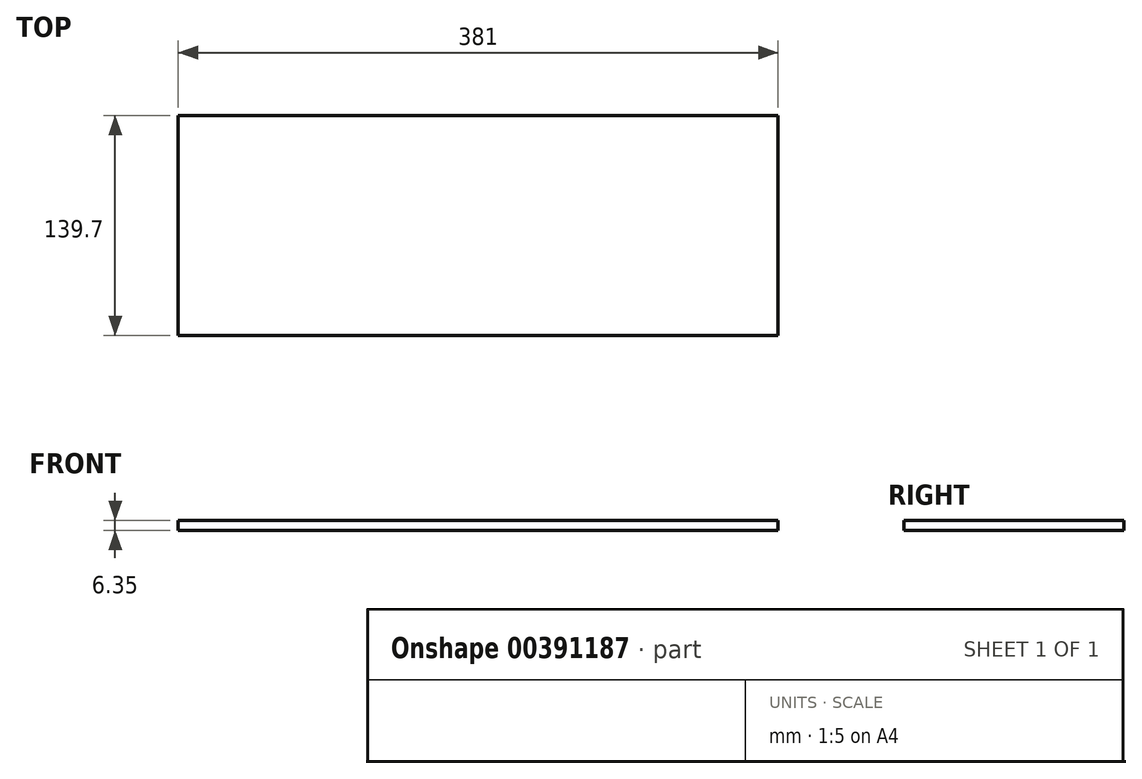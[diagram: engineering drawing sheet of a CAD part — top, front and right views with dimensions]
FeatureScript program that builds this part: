
annotation { "Feature Type Name" : "Feature", "Feature Type Description" : "" }
export const myFeature = defineFeature(function(context is Context, id is Id, definition is map)
    precondition{}
    {
        {
            var Q0;
            Q0=qCreatedBy(makeId("Top.planeOp"),FACE);
            var sketch = newSketch(context, id + "F0", { "sketchPlane" : qUnion([Q0])});
            skLineSegment(sketch, "E0.bottom", {"start": v(190.5, -69.85) * mm, "end": v(-190.5, -69.85) * mm});
            skLineSegment(sketch, "E0.top", {"start": v(190.5, 69.85) * mm, "end": v(-190.5, 69.85) * mm});
            skLineSegment(sketch, "E0.left", {"start": v(190.5, -69.85) * mm, "end": v(190.5, 69.85) * mm});
            skLineSegment(sketch, "E0.right", {"start": v(-190.5, -69.85) * mm, "end": v(-190.5, 69.85) * mm});
            skPoint(sketch, "E0.middle", {"position": v(0, 0) * mm});
            skSolve(sketch);
        }
        {
            var Q0;
            Q0=makeQuery(id+"F0.imprint","IMPRINT",FACE,{"disambiguationData":[TD([[makeQuery(id+"F0.imprint","IMPRINT",EDGE,{"derivedFrom":sQuery(id+"F0.wireOp",EDGE,"E0.bottom")}),-1.0]])]});
            extrude(context, id + "F1", {"entities" : qUnion([Q0]), "depth" : 6.35 * mm});
        }
    });
